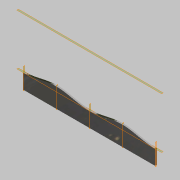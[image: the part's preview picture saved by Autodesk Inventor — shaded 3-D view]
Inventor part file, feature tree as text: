
AUTODESK INVENTOR PART (.ipt)
format: ipt  version: 2017.3 (Build 213257000, 257)  size: 168,960 bytes
history: native  units: in
note: dims shown in document units (in); Inventor stores cm internally (conversion verified against a paired STEP export)
features: plane x7, extrude x2, sketch x2, other x2
ambient origin geometry x8: Origin, YZ Plane, XZ Plane, XY Plane, X Axis, Y Axis, Z Axis, Center Point
bodies: Solid1 (feature_tree)
feature tree (13):
  extrude  "Extrusion1"  Depth=0.5in TaperAngle=0.0deg
  extrude  "Extrusion2"  Depth=0.001in TaperAngle=0.0deg
  plane  "Work Plane1 Centerline at surface"
  plane  "Work Plane2 Centerline at centerline"
  plane  "Work Plane3 Top"
  plane  "Work Plane4 Right"
  plane  "Work Plane5 Bottom"
  plane  "Work Plane6 Left"
  plane  "Work Plane7 Top"
  sketch  "Sketch1"  dims[d0=0.0in d1=17.3159in d2=0.5in d3=0.0in]
  other  "2D Equation Curve1"
  sketch  "Sketch2"  dims[d4=0.0in d5=17.3159in d6=0.001in d7=0.0in d8=-4.9481in d9=-21.9481in d10=0.0in d11=-10.9956in d12=-21.9911in d13=-32.9867in d14=0.0in]
  other  "2D Equation Curve2"
